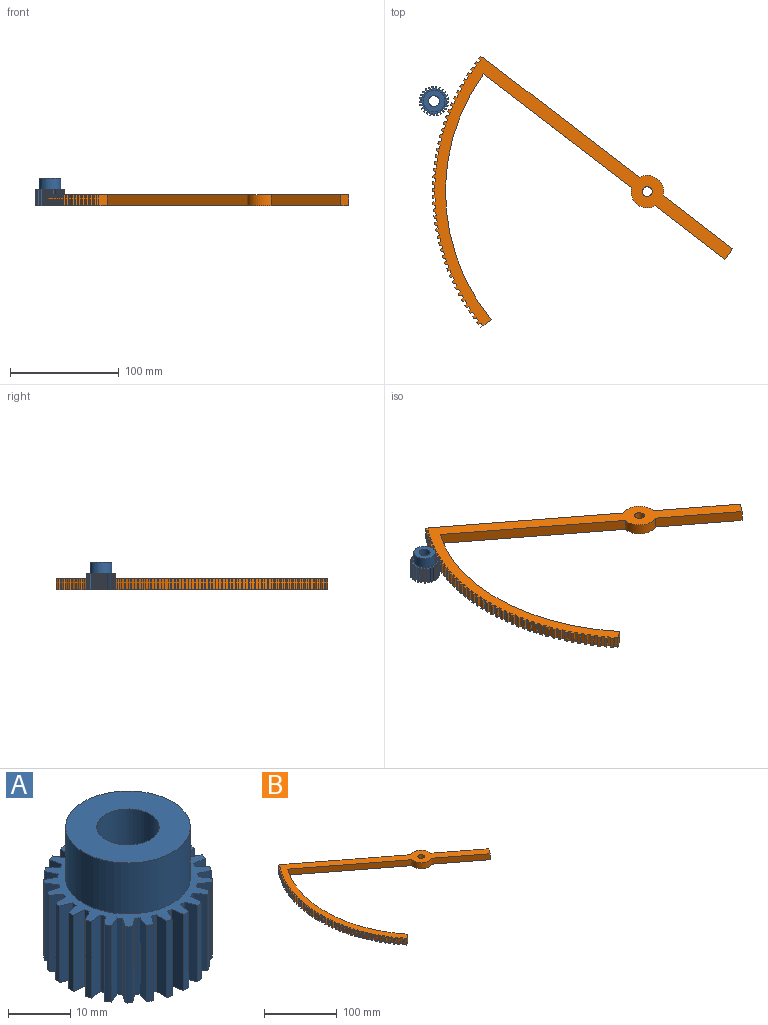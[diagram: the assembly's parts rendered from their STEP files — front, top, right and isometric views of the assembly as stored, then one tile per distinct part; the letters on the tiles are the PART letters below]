
ASSEMBLY  parts=2 mates=1
PART A: 105 faces, bbox 27x27x25 mm
  f0: plane 26.99x26.97mm, normal (0,0,1), area 170.9mm2, adj f1,f2,f3,f4,f5,f6,f7,f8
  f1: cylinder r=13.5mm len=15mm, axis (0,0,-1), area 17.7mm2, adj f0,f26,f30,f103
  f2: cylinder r=13.5mm len=15mm, axis (0,0,-1), area 17.7mm2, adj f0,f26,f100,f102
  f3: cylinder r=13.5mm len=15mm, axis (0,0,-1), area 17.7mm2, adj f0,f26,f97,f99
  f4: cylinder r=13.5mm len=15mm, axis (0,0,-1), area 17.7mm2, adj f0,f26,f94,f96
  f5: cylinder r=13.5mm len=15mm, axis (0,0,-1), area 17.7mm2, adj f0,f26,f91,f93
  f6: cylinder r=13.5mm len=15mm, axis (0,0,-1), area 17.7mm2, adj f0,f26,f88,f90
  f7: cylinder r=13.5mm len=15mm, axis (0,0,-1), area 17.7mm2, adj f0,f26,f85,f87
  f8: cylinder r=13.5mm len=15mm, axis (0,0,-1), area 17.7mm2, adj f0,f26,f82,f84
  f9: cylinder r=13.5mm len=15mm, axis (0,0,-1), area 17.7mm2, adj f0,f26,f79,f81
  f10: cylinder r=13.5mm len=15mm, axis (0,0,-1), area 17.7mm2, adj f0,f26,f76,f78
  f11: cylinder r=13.5mm len=15mm, axis (0,0,-1), area 17.7mm2, adj f0,f26,f73,f75
  f12: cylinder r=13.5mm len=15mm, axis (0,0,-1), area 17.7mm2, adj f0,f26,f70,f72
  f13: cylinder r=13.5mm len=15mm, axis (0,0,-1), area 17.7mm2, adj f0,f26,f67,f69
  f14: cylinder r=13.5mm len=15mm, axis (0,0,-1), area 17.7mm2, adj f0,f26,f64,f66
  f15: cylinder r=13.5mm len=15mm, axis (0,0,-1), area 17.7mm2, adj f0,f26,f61,f63
  f16: cylinder r=13.5mm len=15mm, axis (0,0,-1), area 17.7mm2, adj f0,f26,f58,f60
  f17: cylinder r=13.5mm len=15mm, axis (0,0,-1), area 17.7mm2, adj f0,f26,f55,f57
  f18: cylinder r=13.5mm len=15mm, axis (0,0,-1), area 17.7mm2, adj f0,f26,f52,f54
  f19: cylinder r=13.5mm len=15mm, axis (0,0,-1), area 17.7mm2, adj f0,f26,f49,f51
  f20: cylinder r=13.5mm len=15mm, axis (0,0,-1), area 17.7mm2, adj f0,f26,f46,f48
  f21: cylinder r=13.5mm len=15mm, axis (0,0,-1), area 17.7mm2, adj f0,f26,f43,f45
  f22: cylinder r=13.5mm len=15mm, axis (0,0,-1), area 17.7mm2, adj f0,f26,f40,f42
  f23: cylinder r=13.5mm len=15mm, axis (0,0,-1), area 17.7mm2, adj f0,f26,f37,f39
  f24: cylinder r=13.5mm len=15mm, axis (0,0,-1), area 17.7mm2, adj f0,f26,f34,f36
  f25: cylinder r=13.5mm len=15mm, axis (0,0,-1), area 17.7mm2, adj f0,f26,f31,f33
  f26: plane 26.99x26.97mm, normal (0,0,-1), area 406.5mm2, adj f1,f2,f3,f4,f5,f6,f7,f8
  f27: cylinder r=10mm len=20mm, axis (0,0,-1), area 628.3mm2, adj f0,f28
  f28: plane 20x20mm, normal (0,0,1), area 235.6mm2, adj f27,f29
  f29: cylinder r=5mm len=25mm, axis (0,0,1), area 785.4mm2, adj f26,f28
  f30: plane 15x2.26mm, normal (-0.22,0.97,0), area 34.8mm2, adj f0,f1,f26,f32
  f31: plane 15x2.16mm, normal (-0.35,-0.94,0), area 34.5mm2, adj f0,f25,f26,f32
  f32: plane 15x0.89mm, normal (-1,0.09,0), area 13.4mm2, adj f0,f26,f30,f31
  f33: plane 15x2.32mm, normal (0.02,1,0), area 34.8mm2, adj f0,f25,f26,f35
  f34: plane 15x1.89mm, normal (-0.57,-0.82,0), area 34.5mm2, adj f0,f24,f26,f35
  f35: plane 15x0.84mm, normal (-0.94,0.33,0), area 13.4mm2, adj f0,f26,f33,f34
  f36: plane 15x2.23mm, normal (0.27,0.96,0), area 34.8mm2, adj f0,f24,f26,f38
  f37: plane 15x1.74mm, normal (-0.75,-0.66,0), area 34.5mm2, adj f0,f23,f26,f38
  f38: plane 15x0.74mm, normal (-0.83,0.56,0), area 13.4mm2, adj f0,f26,f36,f37
  f39: plane 15x2.01mm, normal (0.5,0.86,0), area 34.8mm2, adj f0,f23,f26,f41
  f40: plane 15x2.06mm, normal (-0.89,-0.45,0), area 34.5mm2, adj f0,f22,f26,f41
  f41: plane 15x0.66mm, normal (-0.67,0.74,0), area 13.4mm2, adj f0,f26,f39,f40
  f42: plane 15x1.65mm, normal (0.7,0.71,0), area 34.8mm2, adj f0,f22,f26,f44
  f43: plane 15x2.25mm, normal (-0.98,-0.21,0), area 34.5mm2, adj f0,f21,f26,f44
  f44: plane 15x0.79mm, normal (-0.46,0.89,0), area 13.4mm2, adj f0,f26,f42,f43
  f45: plane 15x1.99mm, normal (0.86,0.52,0), area 34.8mm2, adj f0,f21,f26,f47
  f46: plane 15x2.3mm, normal (-1,0.04,0), area 34.5mm2, adj f0,f20,f26,f47
  f47: plane 15x0.87mm, normal (-0.23,0.97,0), area 13.4mm2, adj f0,f26,f45,f46
  f48: plane 15x2.23mm, normal (0.96,0.29,0), area 34.8mm2, adj f0,f20,f26,f50
  f49: plane 15x2.2mm, normal (-0.96,0.29,0), area 34.5mm2, adj f0,f19,f26,f50
  f50: plane 15x0.89mm, normal (0.02,1,0), area 13.4mm2, adj f0,f26,f48,f49
  f51: plane 15x2.32mm, normal (1,0.04,0), area 34.8mm2, adj f0,f19,f26,f53
  f52: plane 15x1.97mm, normal (-0.86,0.52,0), area 34.5mm2, adj f0,f18,f26,f53
  f53: plane 15x0.86mm, normal (0.27,0.96,0), area 13.4mm2, adj f0,f26,f51,f52
  f54: plane 15x2.27mm, normal (0.98,-0.21,0), area 34.8mm2, adj f0,f18,f26,f56
  f55: plane 15x1.64mm, normal (-0.7,0.71,0), area 34.5mm2, adj f0,f17,f26,f56
  f56: plane 15x0.77mm, normal (0.5,0.86,0), area 13.4mm2, adj f0,f26,f54,f55
  f57: plane 15x2.08mm, normal (0.89,-0.45,0), area 34.8mm2, adj f0,f17,f26,f59
  f58: plane 15x1.99mm, normal (-0.5,0.86,0), area 34.5mm2, adj f0,f16,f26,f59
  f59: plane 15x0.64mm, normal (0.7,0.71,0), area 13.4mm2, adj f0,f26,f57,f58
  f60: plane 15x1.75mm, normal (0.75,-0.66,0), area 34.8mm2, adj f0,f16,f26,f62
  f61: plane 15x2.21mm, normal (-0.27,0.96,0), area 34.5mm2, adj f0,f15,f26,f62
  f62: plane 15x0.76mm, normal (0.86,0.52,0), area 13.4mm2, adj f0,f26,f60,f61
  f63: plane 15x1.91mm, normal (0.57,-0.82,0), area 34.8mm2, adj f0,f15,f26,f65
  f64: plane 15x2.3mm, normal (-0.02,1,0), area 34.5mm2, adj f0,f14,f26,f65
  f65: plane 15x0.85mm, normal (0.96,0.29,0), area 13.4mm2, adj f0,f26,f63,f64
  f66: plane 15x2.18mm, normal (0.35,-0.94,0), area 34.8mm2, adj f0,f14,f26,f68
  f67: plane 15x2.24mm, normal (0.22,0.97,0), area 34.5mm2, adj f0,f13,f26,f68
  f68: plane 15x0.89mm, normal (1,0.04,0), area 13.4mm2, adj f0,f26,f66,f67
  f69: plane 15x2.31mm, normal (0.1,-0.99,0), area 34.8mm2, adj f0,f13,f26,f71
  f70: plane 15x2.04mm, normal (0.46,0.89,0), area 34.5mm2, adj f0,f12,f26,f71
  f71: plane 15x0.87mm, normal (0.98,-0.21,0), area 13.4mm2, adj f0,f26,f69,f70
  f72: plane 15x2.3mm, normal (-0.15,-0.99,0), area 34.8mm2, adj f0,f12,f26,f74
  f73: plane 15x1.71mm, normal (0.67,0.75,0), area 34.5mm2, adj f0,f11,f26,f74
  f74: plane 15x0.8mm, normal (0.89,-0.45,0), area 13.4mm2, adj f0,f26,f72,f73
  f75: plane 15x2.14mm, normal (-0.39,-0.92,0), area 34.8mm2, adj f0,f11,f26,f77
  f76: plane 15x1.91mm, normal (0.83,0.56,0), area 34.5mm2, adj f0,f10,f26,f77
  f77: plane 15x0.67mm, normal (0.76,-0.66,0), area 13.4mm2, adj f0,f26,f75,f76
  f78: plane 15x1.84mm, normal (-0.61,-0.79,0), area 34.8mm2, adj f0,f10,f26,f80
  f79: plane 15x2.17mm, normal (0.94,0.33,0), area 34.5mm2, adj f0,f9,f26,f80
  f80: plane 15x0.73mm, normal (0.57,-0.82,0), area 13.4mm2, adj f0,f26,f78,f79
  f81: plane 15x1.82mm, normal (-0.79,-0.62,0), area 34.8mm2, adj f0,f9,f26,f83
  f82: plane 15x2.29mm, normal (1,0.09,0), area 34.5mm2, adj f0,f8,f26,f83
  f83: plane 15x0.84mm, normal (0.35,-0.94,0), area 13.4mm2, adj f0,f26,f81,f82
  f84: plane 15x2.12mm, normal (-0.91,-0.4,0), area 34.8mm2, adj f0,f8,f26,f86
  f85: plane 15x2.27mm, normal (0.99,-0.16,0), area 34.5mm2, adj f0,f7,f26,f86
  f86: plane 15x0.89mm, normal (0.1,-0.99,0), area 13.4mm2, adj f0,f26,f84,f85
  f87: plane 15x2.29mm, normal (-0.99,-0.16,0), area 34.8mm2, adj f0,f7,f26,f89
  f88: plane 15x2.1mm, normal (0.91,-0.4,0), area 34.5mm2, adj f0,f6,f26,f89
  f89: plane 15x0.88mm, normal (-0.15,-0.99,0), area 13.4mm2, adj f0,f26,f87,f88
  f90: plane 15x2.31mm, normal (-1,0.09,0), area 34.8mm2, adj f0,f6,f26,f92
  f91: plane 15x1.81mm, normal (0.79,-0.62,0), area 34.5mm2, adj f0,f5,f26,f92
  f92: plane 15x0.82mm, normal (-0.39,-0.92,0), area 13.4mm2, adj f0,f26,f90,f91
  f93: plane 15x2.19mm, normal (-0.94,0.33,0), area 34.8mm2, adj f0,f5,f26,f95
  f94: plane 15x1.83mm, normal (0.61,-0.79,0), area 34.5mm2, adj f0,f4,f26,f95
  f95: plane 15x0.71mm, normal (-0.61,-0.8,0), area 13.4mm2, adj f0,f26,f93,f94
  f96: plane 15x1.93mm, normal (-0.83,0.56,0), area 34.8mm2, adj f0,f4,f26,f98
  f97: plane 15x2.12mm, normal (0.39,-0.92,0), area 34.5mm2, adj f0,f3,f26,f98
  f98: plane 15x0.7mm, normal (-0.79,-0.62,0), area 13.4mm2, adj f0,f26,f96,f97
  f99: plane 15x1.73mm, normal (-0.67,0.75,0), area 34.8mm2, adj f0,f3,f26,f101
  f100: plane 15x2.27mm, normal (0.15,-0.99,0), area 34.5mm2, adj f0,f2,f26,f101
  f101: plane 15x0.82mm, normal (-0.91,-0.4,0), area 13.4mm2, adj f0,f26,f99,f100
  f102: plane 15x2.06mm, normal (-0.46,0.89,0), area 34.8mm2, adj f0,f2,f26,f104
  f103: plane 15x2.29mm, normal (-0.1,-0.99,0), area 34.5mm2, adj f0,f1,f26,f104
  f104: plane 15x0.88mm, normal (-0.99,-0.16,0), area 13.4mm2, adj f0,f26,f102,f103
PART B: 187 faces, bbox 276.7x249.8x10 mm
  f0: plane 276.65x249.78mm, normal (0,0,1), area 6492mm2, adj f2,f3,f4,f5,f6,f7,f8,f9
  f1: plane 276.65x249.78mm, normal (0,0,-1), area 6492mm2, adj f2,f3,f4,f5,f6,f7,f8,f9
  f2: plane 144.32x110.74mm, normal (0.61,0.79,0), area 1819.1mm2, adj f0,f1,f53,f186
  f3: cylinder r=198mm len=10mm, axis (0,0,-1), area 24.2mm2, adj f0,f1,f58,f185
  f4: cylinder r=198mm len=10mm, axis (0,0,-1), area 1.1mm2, adj f0,f1,f49,f182
  f5: cylinder r=198mm len=10mm, axis (0,0,-1), area 24.2mm2, adj f0,f1,f179,f184
  f6: cylinder r=198mm len=10mm, axis (0,0,-1), area 24.2mm2, adj f0,f1,f176,f181
  f7: cylinder r=198mm len=10mm, axis (0,0,-1), area 24.2mm2, adj f0,f1,f173,f178
  f8: cylinder r=198mm len=10mm, axis (0,0,-1), area 24.2mm2, adj f0,f1,f170,f175
  f9: cylinder r=198mm len=10mm, axis (0,0,-1), area 24.2mm2, adj f0,f1,f167,f172
  f10: cylinder r=198mm len=10mm, axis (0,0,-1), area 24.2mm2, adj f0,f1,f164,f169
  f11: cylinder r=198mm len=10mm, axis (0,0,-1), area 24.2mm2, adj f0,f1,f161,f166
  f12: cylinder r=198mm len=10mm, axis (0,0,-1), area 24.2mm2, adj f0,f1,f158,f163
  f13: cylinder r=198mm len=10mm, axis (0,0,-1), area 24.2mm2, adj f0,f1,f155,f160
  f14: cylinder r=198mm len=10mm, axis (0,0,-1), area 24.2mm2, adj f0,f1,f152,f157
  f15: cylinder r=198mm len=10mm, axis (0,0,-1), area 24.2mm2, adj f0,f1,f149,f154
  f16: cylinder r=198mm len=10mm, axis (0,0,-1), area 24.2mm2, adj f0,f1,f146,f151
  f17: cylinder r=198mm len=10mm, axis (0,0,-1), area 24.2mm2, adj f0,f1,f143,f148
  f18: cylinder r=198mm len=10mm, axis (0,0,-1), area 24.2mm2, adj f0,f1,f140,f145
  f19: cylinder r=198mm len=10mm, axis (0,0,-1), area 24.2mm2, adj f0,f1,f137,f142
  f20: cylinder r=198mm len=10mm, axis (0,0,-1), area 24.2mm2, adj f0,f1,f134,f139
  f21: cylinder r=198mm len=10mm, axis (0,0,-1), area 24.2mm2, adj f0,f1,f131,f136
  f22: cylinder r=198mm len=10mm, axis (0,0,-1), area 24.2mm2, adj f0,f1,f128,f133
  f23: cylinder r=198mm len=10mm, axis (0,0,-1), area 24.2mm2, adj f0,f1,f125,f130
  f24: cylinder r=198mm len=10mm, axis (0,0,-1), area 24.2mm2, adj f0,f1,f122,f127
  f25: cylinder r=198mm len=10mm, axis (0,0,-1), area 24.2mm2, adj f0,f1,f119,f124
  f26: cylinder r=198mm len=10mm, axis (0,0,-1), area 24.2mm2, adj f0,f1,f116,f121
  f27: cylinder r=198mm len=10mm, axis (0,0,-1), area 24.2mm2, adj f0,f1,f113,f118
  f28: cylinder r=198mm len=10mm, axis (0,0,-1), area 24.2mm2, adj f0,f1,f110,f115
  f29: cylinder r=198mm len=10mm, axis (0,0,-1), area 24.2mm2, adj f0,f1,f107,f112
  f30: cylinder r=198mm len=10mm, axis (0,0,-1), area 24.2mm2, adj f0,f1,f104,f109
  f31: cylinder r=198mm len=10mm, axis (0,0,-1), area 24.2mm2, adj f0,f1,f101,f106
  f32: cylinder r=198mm len=10mm, axis (0,0,-1), area 24.2mm2, adj f0,f1,f98,f103
  f33: cylinder r=198mm len=10mm, axis (0,0,-1), area 24.2mm2, adj f0,f1,f95,f100
  f34: cylinder r=198mm len=10mm, axis (0,0,-1), area 24.2mm2, adj f0,f1,f92,f97
  f35: cylinder r=198mm len=10mm, axis (0,0,-1), area 24.2mm2, adj f0,f1,f89,f94
  f36: cylinder r=198mm len=10mm, axis (0,0,-1), area 24.2mm2, adj f0,f1,f86,f91
  f37: cylinder r=198mm len=10mm, axis (0,0,-1), area 24.2mm2, adj f0,f1,f83,f88
  f38: cylinder r=198mm len=10mm, axis (0,0,-1), area 24.2mm2, adj f0,f1,f80,f85
  f39: cylinder r=198mm len=10mm, axis (0,0,-1), area 24.2mm2, adj f0,f1,f77,f82
  f40: cylinder r=198mm len=10mm, axis (0,0,-1), area 24.2mm2, adj f0,f1,f74,f79
  f41: cylinder r=198mm len=10mm, axis (0,0,-1), area 24.2mm2, adj f0,f1,f71,f76
  f42: cylinder r=198mm len=10mm, axis (0,0,-1), area 24.2mm2, adj f0,f1,f68,f73
  f43: cylinder r=198mm len=10mm, axis (0,0,-1), area 24.2mm2, adj f0,f1,f65,f70
  f44: cylinder r=198mm len=10mm, axis (0,0,-1), area 24.2mm2, adj f0,f1,f62,f67
  f45: cylinder r=198mm len=10mm, axis (0,0,-1), area 24.2mm2, adj f0,f1,f59,f64
  f46: cylinder r=198mm len=10mm, axis (0,0,-1), area 24.2mm2, adj f0,f1,f56,f61
  f47: plane 136.58x104.8mm, normal (-0.61,-0.79,0), area 1721.6mm2, adj f0,f1,f50,f54
  f48: plane 64.09x49.18mm, normal (0.61,0.79,0), area 807.9mm2, adj f0,f1,f52,f53
  f49: plane 10x9.53mm, normal (0.61,-0.79,0), area 120.1mm2, adj f0,f1,f4,f50
  f50: cylinder r=186mm len=226.34mm, axis (0,0,-1), area 2434.7mm2, adj f0,f1,f47,f49
  f51: plane 64.09x49.18mm, normal (-0.61,-0.79,0), area 807.9mm2, adj f0,f1,f52,f54
  f52: plane 10x9.52mm, normal (0.79,-0.61,0), area 120mm2, adj f0,f1,f48,f51
  f53: cylinder r=15mm len=22.25mm, axis (0,0,1), area 347.8mm2, adj f0,f1,f2,f48
  f54: cylinder r=15mm len=22.25mm, axis (0,0,1), area 347.8mm2, adj f0,f1,f47,f51
  f55: cylinder r=4.5mm len=10mm, axis (0,0,1), area 282.7mm2, adj f0,f1
  f56: plane 10x2.06mm, normal (0.44,0.9,0), area 22.9mm2, adj f0,f1,f46,f57
  f57: cylinder r=195.75mm len=10mm, axis (0,0,1), area 28.6mm2, adj f0,f1,f56,f58
  f58: plane 10x1.8mm, normal (-0.78,-0.63,0), area 23.1mm2, adj f0,f1,f3,f57
  f59: plane 10x2.09mm, normal (0.41,0.91,0), area 22.9mm2, adj f0,f1,f45,f60
  f60: cylinder r=195.75mm len=10mm, axis (0,0,1), area 28.6mm2, adj f0,f1,f59,f61
  f61: plane 10x1.76mm, normal (-0.76,-0.65,0), area 23.1mm2, adj f0,f1,f46,f60
  f62: plane 10x2.12mm, normal (0.38,0.92,0), area 22.9mm2, adj f0,f1,f44,f63
  f63: cylinder r=195.75mm len=10mm, axis (0,0,1), area 28.6mm2, adj f0,f1,f62,f64
  f64: plane 10x1.71mm, normal (-0.74,-0.67,0), area 23.1mm2, adj f0,f1,f45,f63
  f65: plane 10x2.15mm, normal (0.35,0.94,0), area 22.9mm2, adj f0,f1,f43,f66
  f66: cylinder r=195.75mm len=10mm, axis (0,0,1), area 28.6mm2, adj f0,f1,f65,f67
  f67: plane 10x1.66mm, normal (-0.72,-0.7,0), area 23.1mm2, adj f0,f1,f44,f66
  f68: plane 10x2.17mm, normal (0.32,0.95,0), area 22.9mm2, adj f0,f1,f42,f69
  f69: cylinder r=195.75mm len=10mm, axis (0,0,1), area 28.6mm2, adj f0,f1,f68,f70
  f70: plane 10x1.66mm, normal (-0.69,-0.72,0), area 23.1mm2, adj f0,f1,f43,f69
  f71: plane 10x2.19mm, normal (0.29,0.96,0), area 22.9mm2, adj f0,f1,f41,f72
  f72: cylinder r=195.75mm len=10mm, axis (0,0,1), area 28.6mm2, adj f0,f1,f71,f73
  f73: plane 10x1.71mm, normal (-0.67,-0.74,0), area 23.1mm2, adj f0,f1,f42,f72
  f74: plane 10x2.21mm, normal (0.26,0.97,0), area 22.9mm2, adj f0,f1,f40,f75
  f75: cylinder r=195.75mm len=10mm, axis (0,0,1), area 28.6mm2, adj f0,f1,f74,f76
  f76: plane 10x1.76mm, normal (-0.65,-0.76,0), area 23.1mm2, adj f0,f1,f41,f75
  f77: plane 10x2.23mm, normal (0.23,0.97,0), area 22.9mm2, adj f0,f1,f39,f78
  f78: cylinder r=195.75mm len=10mm, axis (0,0,1), area 28.6mm2, adj f0,f1,f77,f79
  f79: plane 10x1.81mm, normal (-0.62,-0.78,0), area 23.1mm2, adj f0,f1,f40,f78
  f80: plane 10x2.25mm, normal (0.2,0.98,0), area 22.9mm2, adj f0,f1,f38,f81
  f81: cylinder r=195.75mm len=10mm, axis (0,0,1), area 28.6mm2, adj f0,f1,f80,f82
  f82: plane 10x1.85mm, normal (-0.6,-0.8,0), area 23.1mm2, adj f0,f1,f39,f81
  f83: plane 10x2.26mm, normal (0.17,0.99,0), area 22.9mm2, adj f0,f1,f37,f84
  f84: cylinder r=195.75mm len=10mm, axis (0,0,1), area 28.6mm2, adj f0,f1,f83,f85
  f85: plane 10x1.89mm, normal (-0.57,-0.82,0), area 23.1mm2, adj f0,f1,f38,f84
  f86: plane 10x2.27mm, normal (0.14,0.99,0), area 22.9mm2, adj f0,f1,f36,f87
  f87: cylinder r=195.75mm len=10mm, axis (0,0,1), area 28.6mm2, adj f0,f1,f86,f88
  f88: plane 10x1.94mm, normal (-0.55,-0.84,0), area 23.1mm2, adj f0,f1,f37,f87
  f89: plane 10x2.28mm, normal (0.11,0.99,0), area 22.9mm2, adj f0,f1,f35,f90
  f90: cylinder r=195.75mm len=10mm, axis (0,0,1), area 28.6mm2, adj f0,f1,f89,f91
  f91: plane 10x1.97mm, normal (-0.52,-0.85,0), area 23.1mm2, adj f0,f1,f36,f90
  f92: plane 10x2.29mm, normal (0.07,1,0), area 22.9mm2, adj f0,f1,f34,f93
  f93: cylinder r=195.75mm len=10mm, axis (0,0,1), area 28.6mm2, adj f0,f1,f92,f94
  f94: plane 10x2.01mm, normal (-0.49,-0.87,0), area 23.1mm2, adj f0,f1,f35,f93
  f95: plane 10x2.29mm, normal (0.04,1,0), area 22.9mm2, adj f0,f1,f33,f96
  f96: cylinder r=195.75mm len=10mm, axis (0,0,1), area 28.6mm2, adj f0,f1,f95,f97
  f97: plane 10x2.05mm, normal (-0.46,-0.89,0), area 23.1mm2, adj f0,f1,f34,f96
  f98: plane 10x2.29mm, normal (0.01,1,0), area 22.9mm2, adj f0,f1,f32,f99
  f99: cylinder r=195.75mm len=10mm, axis (0,0,1), area 28.6mm2, adj f0,f1,f98,f100
  f100: plane 10x2.08mm, normal (-0.44,-0.9,0), area 23.1mm2, adj f0,f1,f33,f99
  f101: plane 10x2.29mm, normal (-0.02,1,0), area 22.9mm2, adj f0,f1,f31,f102
  f102: cylinder r=195.75mm len=10mm, axis (0,0,1), area 28.6mm2, adj f0,f1,f101,f103
  f103: plane 10x2.11mm, normal (-0.41,-0.91,0), area 23.1mm2, adj f0,f1,f32,f102
  f104: plane 10x2.29mm, normal (-0.05,1,0), area 22.9mm2, adj f0,f1,f30,f105
  f105: cylinder r=195.75mm len=10mm, axis (0,0,1), area 28.6mm2, adj f0,f1,f104,f106
  f106: plane 10x2.14mm, normal (-0.38,-0.93,0), area 23.1mm2, adj f0,f1,f31,f105
  f107: plane 10x2.29mm, normal (-0.08,1,0), area 22.9mm2, adj f0,f1,f29,f108
  f108: cylinder r=195.75mm len=10mm, axis (0,0,1), area 28.6mm2, adj f0,f1,f107,f109
  f109: plane 10x2.17mm, normal (-0.35,-0.94,0), area 23.1mm2, adj f0,f1,f30,f108
  f110: plane 10x2.28mm, normal (-0.12,0.99,0), area 22.9mm2, adj f0,f1,f28,f111
  f111: cylinder r=195.75mm len=10mm, axis (0,0,1), area 28.6mm2, adj f0,f1,f110,f112
  f112: plane 10x2.19mm, normal (-0.32,-0.95,0), area 23.1mm2, adj f0,f1,f29,f111
  f113: plane 10x2.27mm, normal (-0.15,0.99,0), area 22.9mm2, adj f0,f1,f27,f114
  f114: cylinder r=195.75mm len=10mm, axis (0,0,1), area 28.6mm2, adj f0,f1,f113,f115
  f115: plane 10x2.21mm, normal (-0.29,-0.96,0), area 23.1mm2, adj f0,f1,f28,f114
  f116: plane 10x2.26mm, normal (-0.18,0.98,0), area 22.9mm2, adj f0,f1,f26,f117
  f117: cylinder r=195.75mm len=10mm, axis (0,0,1), area 28.6mm2, adj f0,f1,f116,f118
  f118: plane 10x2.23mm, normal (-0.26,-0.97,0), area 23.1mm2, adj f0,f1,f27,f117
  f119: plane 10x2.24mm, normal (-0.21,0.98,0), area 22.9mm2, adj f0,f1,f25,f120
  f120: cylinder r=195.75mm len=10mm, axis (0,0,1), area 28.6mm2, adj f0,f1,f119,f121
  f121: plane 10x2.25mm, normal (-0.23,-0.97,0), area 23.1mm2, adj f0,f1,f26,f120
  f122: plane 10x2.23mm, normal (-0.24,0.97,0), area 22.9mm2, adj f0,f1,f24,f123
  f123: cylinder r=195.75mm len=10mm, axis (0,0,1), area 28.6mm2, adj f0,f1,f122,f124
  f124: plane 10x2.27mm, normal (-0.2,-0.98,0), area 23.1mm2, adj f0,f1,f25,f123
  f125: plane 10x2.21mm, normal (-0.27,0.96,0), area 22.9mm2, adj f0,f1,f23,f126
  f126: cylinder r=195.75mm len=10mm, axis (0,0,1), area 28.6mm2, adj f0,f1,f125,f127
  f127: plane 10x2.28mm, normal (-0.16,-0.99,0), area 23.1mm2, adj f0,f1,f24,f126
  f128: plane 10x2.19mm, normal (-0.3,0.95,0), area 22.9mm2, adj f0,f1,f22,f129
  f129: cylinder r=195.75mm len=10mm, axis (0,0,1), area 28.6mm2, adj f0,f1,f128,f130
  f130: plane 10x2.29mm, normal (-0.13,-0.99,0), area 23.1mm2, adj f0,f1,f23,f129
  f131: plane 10x2.16mm, normal (-0.33,0.94,0), area 22.9mm2, adj f0,f1,f21,f132
  f132: cylinder r=195.75mm len=10mm, axis (0,0,1), area 28.6mm2, adj f0,f1,f131,f133
  f133: plane 10x2.3mm, normal (-0.1,-0.99,0), area 23.1mm2, adj f0,f1,f22,f132
  f134: plane 10x2.14mm, normal (-0.36,0.93,0), area 22.9mm2, adj f0,f1,f20,f135
  f135: cylinder r=195.75mm len=10mm, axis (0,0,1), area 28.6mm2, adj f0,f1,f134,f136
  f136: plane 10x2.3mm, normal (-0.07,-1,0), area 23.1mm2, adj f0,f1,f21,f135
  f137: plane 10x2.11mm, normal (-0.39,0.92,0), area 22.9mm2, adj f0,f1,f19,f138
  f138: cylinder r=195.75mm len=10mm, axis (0,0,1), area 28.6mm2, adj f0,f1,f137,f139
  f139: plane 10x2.31mm, normal (-0.04,-1,0), area 23.1mm2, adj f0,f1,f20,f138
  f140: plane 10x2.08mm, normal (-0.42,0.91,0), area 22.9mm2, adj f0,f1,f18,f141
  f141: cylinder r=195.75mm len=10mm, axis (0,0,1), area 28.6mm2, adj f0,f1,f140,f142
  f142: plane 10x2.31mm, normal (-0.01,-1,0), area 23.1mm2, adj f0,f1,f19,f141
  f143: plane 10x2.05mm, normal (-0.45,0.89,0), area 22.9mm2, adj f0,f1,f17,f144
  f144: cylinder r=195.75mm len=10mm, axis (0,0,1), area 28.6mm2, adj f0,f1,f143,f145
  f145: plane 10x2.31mm, normal (0.03,-1,0), area 23.1mm2, adj f0,f1,f18,f144
  f146: plane 10x2.02mm, normal (-0.48,0.88,0), area 22.9mm2, adj f0,f1,f16,f147
  f147: cylinder r=195.75mm len=10mm, axis (0,0,1), area 28.6mm2, adj f0,f1,f146,f148
  f148: plane 10x2.31mm, normal (0.06,-1,0), area 23.1mm2, adj f0,f1,f17,f147
  f149: plane 10x1.98mm, normal (-0.5,0.86,0), area 22.9mm2, adj f0,f1,f15,f150
  f150: cylinder r=195.75mm len=10mm, axis (0,0,1), area 28.6mm2, adj f0,f1,f149,f151
  f151: plane 10x2.3mm, normal (0.09,-1,0), area 23.1mm2, adj f0,f1,f16,f150
  f152: plane 10x1.94mm, normal (-0.53,0.85,0), area 22.9mm2, adj f0,f1,f14,f153
  f153: cylinder r=195.75mm len=10mm, axis (0,0,1), area 28.6mm2, adj f0,f1,f152,f154
  f154: plane 10x2.29mm, normal (0.12,-0.99,0), area 23.1mm2, adj f0,f1,f15,f153
  f155: plane 10x1.9mm, normal (-0.56,0.83,0), area 22.9mm2, adj f0,f1,f13,f156
  f156: cylinder r=195.75mm len=10mm, axis (0,0,1), area 28.6mm2, adj f0,f1,f155,f157
  f157: plane 10x2.28mm, normal (0.15,-0.99,0), area 23.1mm2, adj f0,f1,f14,f156
  f158: plane 10x1.86mm, normal (-0.58,0.81,0), area 22.9mm2, adj f0,f1,f12,f159
  f159: cylinder r=195.75mm len=10mm, axis (0,0,1), area 28.6mm2, adj f0,f1,f158,f160
  f160: plane 10x2.27mm, normal (0.18,-0.98,0), area 23.1mm2, adj f0,f1,f13,f159
  f161: plane 10x1.82mm, normal (-0.61,0.79,0), area 22.9mm2, adj f0,f1,f11,f162
  f162: cylinder r=195.75mm len=10mm, axis (0,0,1), area 28.6mm2, adj f0,f1,f161,f163
  f163: plane 10x2.26mm, normal (0.21,-0.98,0), area 23.1mm2, adj f0,f1,f12,f162
  f164: plane 10x1.77mm, normal (-0.63,0.77,0), area 22.9mm2, adj f0,f1,f10,f165
  f165: cylinder r=195.75mm len=10mm, axis (0,0,1), area 28.6mm2, adj f0,f1,f164,f166
  f166: plane 10x2.24mm, normal (0.24,-0.97,0), area 23.1mm2, adj f0,f1,f11,f165
  f167: plane 10x1.73mm, normal (-0.66,0.75,0), area 22.9mm2, adj f0,f1,f9,f168
  f168: cylinder r=195.75mm len=10mm, axis (0,0,1), area 28.6mm2, adj f0,f1,f167,f169
  f169: plane 10x2.22mm, normal (0.28,-0.96,0), area 23.1mm2, adj f0,f1,f10,f168
  f170: plane 10x1.68mm, normal (-0.68,0.73,0), area 22.9mm2, adj f0,f1,f8,f171
  f171: cylinder r=195.75mm len=10mm, axis (0,0,1), area 28.6mm2, adj f0,f1,f170,f172
  f172: plane 10x2.2mm, normal (0.31,-0.95,0), area 23.1mm2, adj f0,f1,f9,f171
  f173: plane 10x1.63mm, normal (-0.7,0.71,0), area 22.9mm2, adj f0,f1,f7,f174
  f174: cylinder r=195.75mm len=10mm, axis (0,0,1), area 28.6mm2, adj f0,f1,f173,f175
  f175: plane 10x2.18mm, normal (0.34,-0.94,0), area 23.1mm2, adj f0,f1,f8,f174
  f176: plane 10x1.67mm, normal (-0.73,0.69,0), area 22.9mm2, adj f0,f1,f6,f177
  f177: cylinder r=195.75mm len=10mm, axis (0,0,1), area 28.6mm2, adj f0,f1,f176,f178
  f178: plane 10x2.15mm, normal (0.37,-0.93,0), area 23.1mm2, adj f0,f1,f7,f177
  f179: plane 10x1.72mm, normal (-0.75,0.66,0), area 22.9mm2, adj f0,f1,f5,f180
  f180: cylinder r=195.75mm len=10mm, axis (0,0,1), area 28.6mm2, adj f0,f1,f179,f181
  f181: plane 10x2.12mm, normal (0.4,-0.92,0), area 23.1mm2, adj f0,f1,f6,f180
  f182: plane 10x1.76mm, normal (-0.77,0.64,0), area 22.9mm2, adj f0,f1,f4,f183
  f183: cylinder r=195.75mm len=10mm, axis (0,0,1), area 28.6mm2, adj f0,f1,f182,f184
  f184: plane 10x2.09mm, normal (0.42,-0.91,0), area 23.1mm2, adj f0,f1,f5,f183
  f185: plane 10x2.03mm, normal (0.47,0.88,0), area 22.9mm2, adj f0,f1,f3,f186
  f186: cylinder r=195.75mm len=10mm, axis (0,0,1), area 5.2mm2, adj f0,f1,f2,f185
PLACE A t=(-130.54,82.73,-24.15)mm
PLACE B t=(66.02,-0.68,-24.15)mm
MATE planar A.f1 <-> B.f1  axis (0,0,-1) through (-130.54,82.73,-24.15)mm
